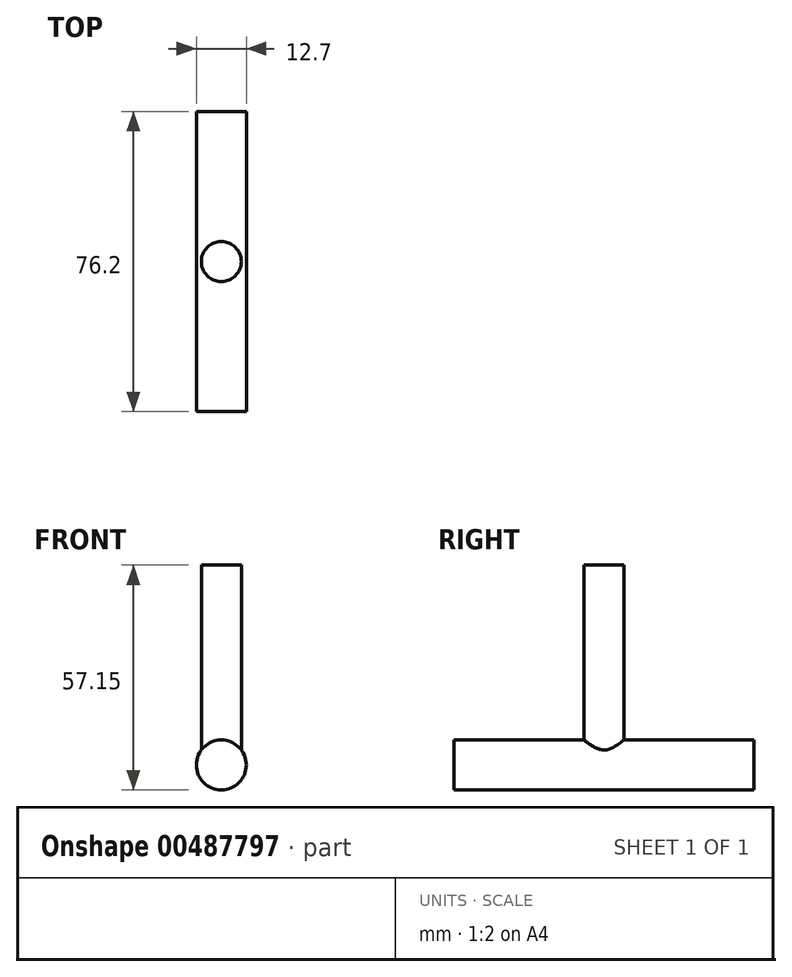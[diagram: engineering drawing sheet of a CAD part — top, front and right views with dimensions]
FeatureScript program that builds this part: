
annotation { "Feature Type Name" : "Feature", "Feature Type Description" : "" }
export const myFeature = defineFeature(function(context is Context, id is Id, definition is map)
    precondition{}
    {
        {
            var Q0;
            Q0=qCreatedBy(makeId("Front.planeOp"),FACE);
            var sketch = newSketch(context, id + "F0", { "sketchPlane" : qUnion([Q0])});
            skCircle(sketch, "E0", {"center": v(0, 0) * mm, "radius": 6.35 * mm});
            skSolve(sketch);
        }
        {
            var Q0;
            Q0=makeQuery(id+"F0.imprint","IMPRINT",FACE,{"disambiguationData":[TD([[makeQuery(id+"F0.imprint","IMPRINT",EDGE,{"derivedFrom":sQuery(id+"F0.wireOp",EDGE,"E0")}),1.0]])]});
            extrude(context, id + "F1", {"entities" : qUnion([Q0]), "endBound" : BoundingType.SYMMETRIC, "depth" : 76.2 * mm});
        }
        {
            var Q0;
            Q0=qCreatedBy(makeId("Top.planeOp"),FACE);
            var sketch = newSketch(context, id + "F2", { "sketchPlane" : qUnion([Q0])});
            skCircle(sketch, "E1", {"center": v(0, 0) * mm, "radius": 5.08 * mm});
            skSolve(sketch);
        }
        {
            var Q0;
            Q0 = qSketchRegion(id + "F2", true);
            extrude(context, id + "F3", {"entities" : qUnion([Q0]), "operationType" : NewBodyOperationType.ADD, "depth" : 50.8 * mm});
        }
    });
